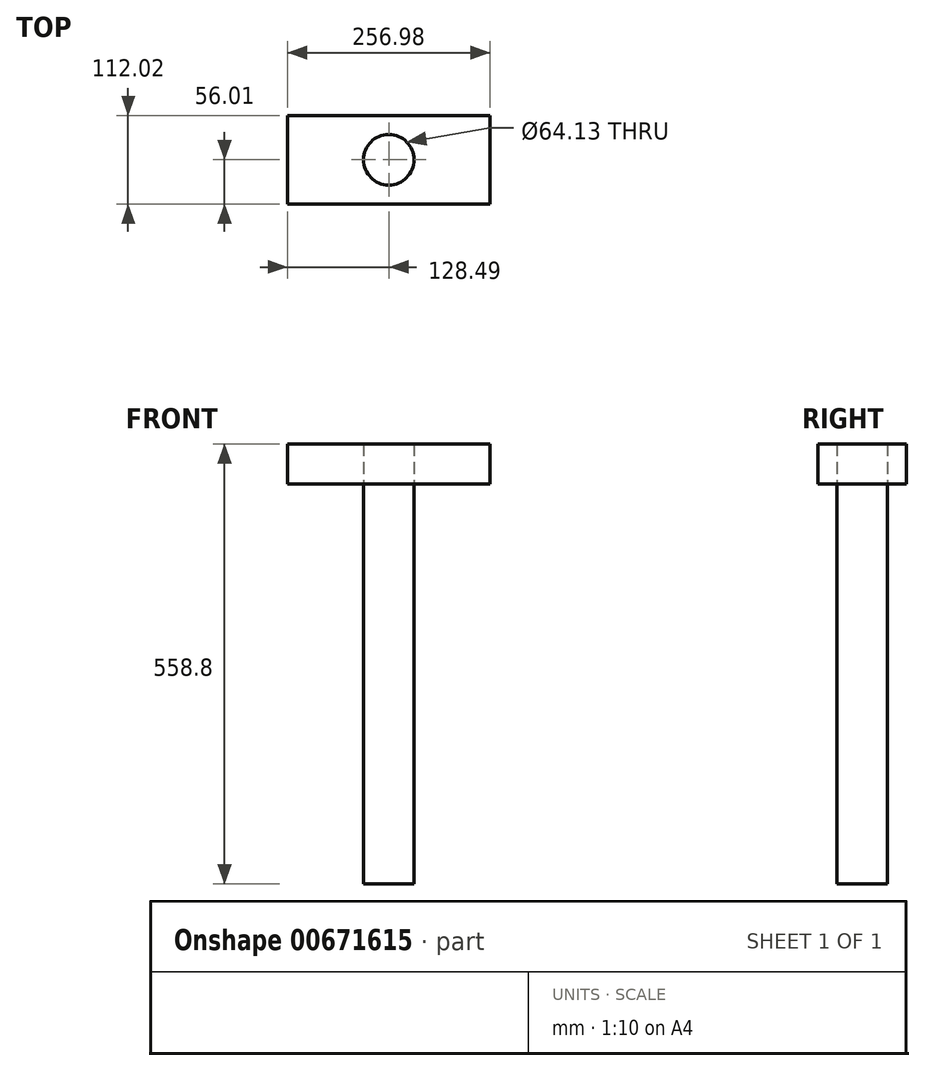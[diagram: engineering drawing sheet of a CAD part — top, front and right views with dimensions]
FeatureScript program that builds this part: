
annotation { "Feature Type Name" : "Feature", "Feature Type Description" : "" }
export const myFeature = defineFeature(function(context is Context, id is Id, definition is map)
    precondition{}
    {
        {
            var Q0;
            Q0=qCreatedBy(makeId("Top.planeOp"),FACE);
            var sketch = newSketch(context, id + "F0", { "sketchPlane" : qUnion([Q0])});
            skCircle(sketch, "E0", {"center": v(0, 0) * mm, "radius": 32.07 * mm});
            skSolve(sketch);
        }
        {
            var Q0;
            Q0=makeQuery(id+"F0.imprint","IMPRINT",FACE,{"disambiguationData":[TD([[makeQuery(id+"F0.imprint","IMPRINT",EDGE,{"derivedFrom":sQuery(id+"F0.wireOp",EDGE,"E0")}),1.0]])]});
            extrude(context, id + "F1", {"entities" : qUnion([Q0]), "depth" : 508 * mm, "offsetDistance" : 25.4 * mm});
        }
        {
            var Q0;
            Q0=makeQuery(id+"F1.opExtrude","CAP_FACE",FACE,{"disambiguationData":[OSD([sQuery(id+"F0.wireOp",EDGE,"E0")])],"isStart":false});
            var sketch = newSketch(context, id + "F2", { "sketchPlane" : qUnion([Q0])});
            skLineSegment(sketch, "E1.bottom", {"start": v(128.5, -56) * mm, "end": v(-128.5, -56) * mm});
            skLineSegment(sketch, "E1.top", {"start": v(128.5, 56) * mm, "end": v(-128.5, 56) * mm});
            skLineSegment(sketch, "E1.left", {"start": v(128.5, -56) * mm, "end": v(128.5, 56) * mm});
            skLineSegment(sketch, "E1.right", {"start": v(-128.5, -56) * mm, "end": v(-128.5, 56) * mm});
            skPoint(sketch, "E1.middle", {"position": v(0, 0) * mm});
            skSolve(sketch);
        }
        {
            var Q0;
            Q0=makeQuery(id+"F2.imprint","IMPRINT",FACE,{"disambiguationData":[TD([[makeQuery(id+"F2.imprint","IMPRINT",EDGE,{"derivedFrom":sQuery(id+"F2.wireOp",EDGE,"E1.bottom")}),-1.0]])]});
            extrude(context, id + "F3", {"entities" : qUnion([Q0]), "depth" : 50.8 * mm, "offsetDistance" : 25.4 * mm});
        }
    });
